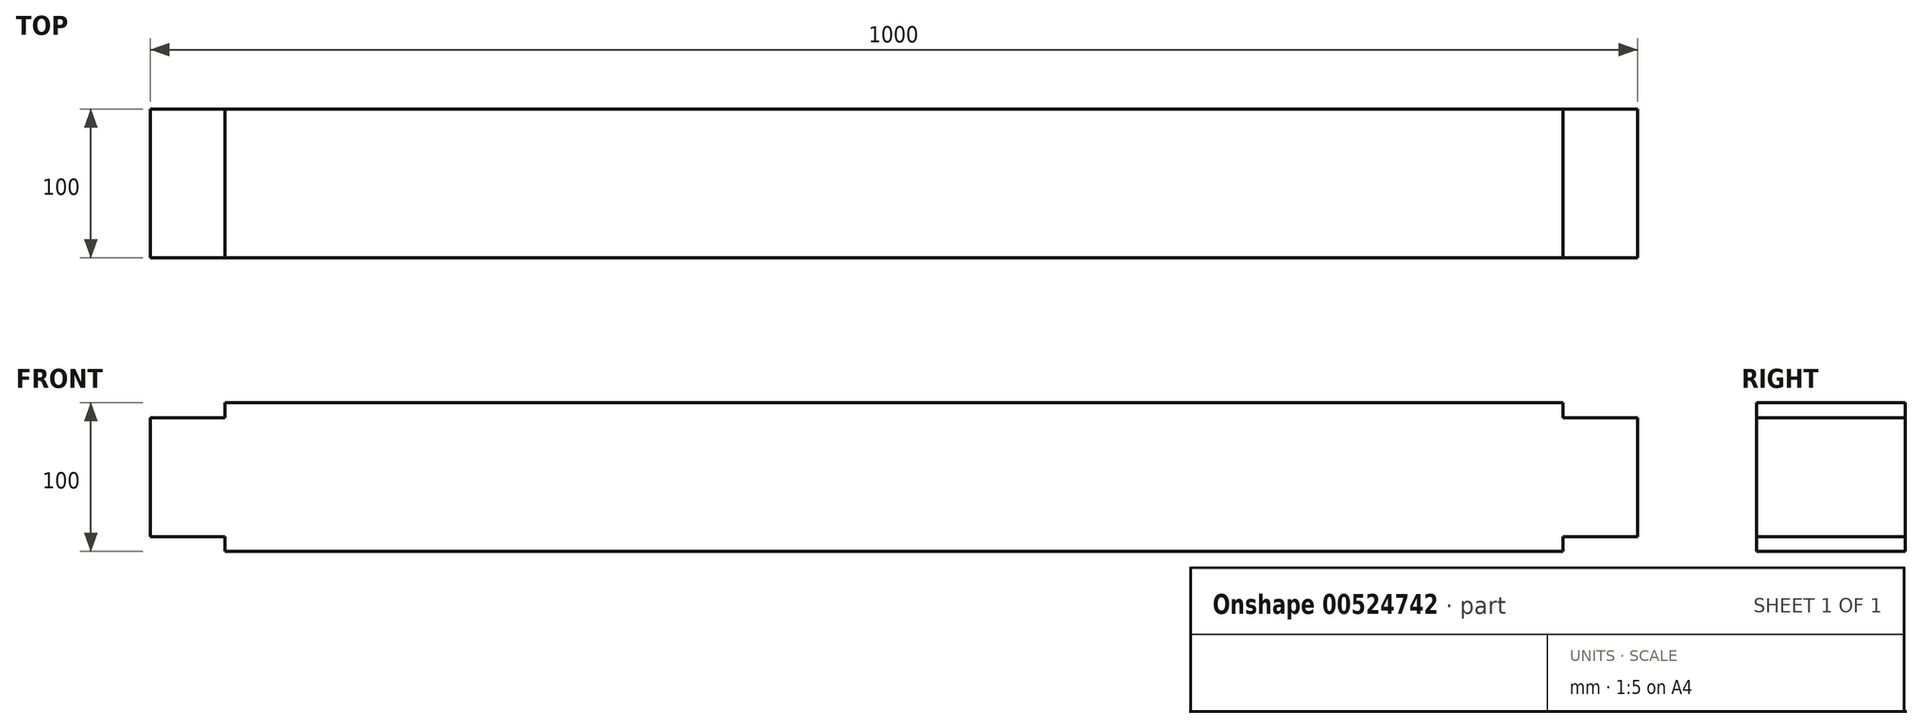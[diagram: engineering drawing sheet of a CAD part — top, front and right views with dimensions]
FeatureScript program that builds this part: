
annotation { "Feature Type Name" : "Feature", "Feature Type Description" : "" }
export const myFeature = defineFeature(function(context is Context, id is Id, definition is map)
    precondition{}
    {
        {
            var Q0;
            Q0=qCreatedBy(makeId("Front.planeOp"),FACE);
            var sketch = newSketch(context, id + "F0", { "sketchPlane" : qUnion([Q0])});
            skLineSegment(sketch, "E0.bottom", {"start": v(-1399.63, 0) * mm, "end": v(-399.63, 0) * mm});
            skLineSegment(sketch, "E0.top", {"start": v(-1399.63, 100) * mm, "end": v(-399.63, 100) * mm});
            skLineSegment(sketch, "E0.left", {"start": v(-1399.63, 0) * mm, "end": v(-1399.63, 100) * mm});
            skLineSegment(sketch, "E0.right", {"start": v(-399.63, 0) * mm, "end": v(-399.63, 100) * mm});
            skSolve(sketch);
        }
        {
            var Q0;
            Q0=makeQuery(id+"F0.imprint","IMPRINT",FACE,{"disambiguationData":[TD([[makeQuery(id+"F0.imprint","IMPRINT",EDGE,{"derivedFrom":sQuery(id+"F0.wireOp",EDGE,"E0.bottom")}),1.0]])]});
            extrude(context, id + "F1", {"entities" : qUnion([Q0]), "depth" : 100 * mm, "offsetDistance" : 25 * mm});
        }
        {
            var Q0;
            Q0=makeQuery(id+"F1.opExtrude","CAP_FACE",FACE,{"disambiguationData":[OSD([sQuery(id+"F0.wireOp",EDGE,"E0.bottom"),sQuery(id+"F0.wireOp",EDGE,"E0.top"),sQuery(id+"F0.wireOp",EDGE,"E0.left"),sQuery(id+"F0.wireOp",EDGE,"E0.right")])],"isStart":false});
            var sketch = newSketch(context, id + "F2", { "sketchPlane" : qUnion([Q0])});
            skLineSegment(sketch, "E1.bottom", {"start": v(-1399.63, 100) * mm, "end": v(-1349.63, 100) * mm});
            skLineSegment(sketch, "E1.top", {"start": v(-1399.63, 90) * mm, "end": v(-1349.63, 90) * mm});
            skLineSegment(sketch, "E1.left", {"start": v(-1399.63, 100) * mm, "end": v(-1399.63, 90) * mm});
            skLineSegment(sketch, "E1.right", {"start": v(-1349.63, 100) * mm, "end": v(-1349.63, 90) * mm});
            skLineSegment(sketch, "E2.bottom", {"start": v(-1399.63, 0) * mm, "end": v(-1349.63, 0) * mm});
            skLineSegment(sketch, "E2.top", {"start": v(-1399.63, 10) * mm, "end": v(-1349.63, 10) * mm});
            skLineSegment(sketch, "E2.left", {"start": v(-1399.63, 0) * mm, "end": v(-1399.63, 10) * mm});
            skLineSegment(sketch, "E2.right", {"start": v(-1349.63, 0) * mm, "end": v(-1349.63, 10) * mm});
            skLineSegment(sketch, "E3.bottom", {"start": v(-399.63, 100) * mm, "end": v(-449.63, 100) * mm});
            skLineSegment(sketch, "E3.top", {"start": v(-399.63, 90) * mm, "end": v(-449.63, 90) * mm});
            skLineSegment(sketch, "E3.left", {"start": v(-399.63, 100) * mm, "end": v(-399.63, 90) * mm});
            skLineSegment(sketch, "E3.right", {"start": v(-449.63, 100) * mm, "end": v(-449.63, 90) * mm});
            skLineSegment(sketch, "E4.bottom", {"start": v(-399.63, 0) * mm, "end": v(-449.63, 0) * mm});
            skLineSegment(sketch, "E4.top", {"start": v(-399.63, 10) * mm, "end": v(-449.63, 10) * mm});
            skLineSegment(sketch, "E4.left", {"start": v(-399.63, 0) * mm, "end": v(-399.63, 10) * mm});
            skLineSegment(sketch, "E4.right", {"start": v(-449.63, 0) * mm, "end": v(-449.63, 10) * mm});
            skSolve(sketch);
        }
        {
            var Q0;
            Q0=makeQuery(id+"F2.imprint","IMPRINT",FACE,{"disambiguationData":[TD([[makeQuery(id+"F2.imprint","IMPRINT",EDGE,{"derivedFrom":sQuery(id+"F2.wireOp",EDGE,"E3.bottom")}),-1.0]])]});
            var Q1;
            Q1=makeQuery(id+"F2.imprint","IMPRINT",FACE,{"disambiguationData":[TD([[makeQuery(id+"F2.imprint","IMPRINT",EDGE,{"derivedFrom":sQuery(id+"F2.wireOp",EDGE,"E4.bottom")}),1.0]])]});
            var Q2;
            Q2=makeQuery(id+"F2.imprint","IMPRINT",FACE,{"disambiguationData":[TD([[makeQuery(id+"F2.imprint","IMPRINT",EDGE,{"derivedFrom":sQuery(id+"F2.wireOp",EDGE,"E1.bottom")}),-1.0]])]});
            var Q3;
            Q3=makeQuery(id+"F2.imprint","IMPRINT",FACE,{"disambiguationData":[TD([[makeQuery(id+"F2.imprint","IMPRINT",EDGE,{"derivedFrom":sQuery(id+"F2.wireOp",EDGE,"E2.bottom")}),1.0]])]});
            extrude(context, id + "F3", {"entities" : qUnion([Q0, Q1, Q2, Q3]), "operationType" : NewBodyOperationType.REMOVE, "endBound" : BoundingType.THROUGH_ALL, "oppositeDirection" : true, "depth" : 25 * mm, "offsetDistance" : 25 * mm});
        }
    });
